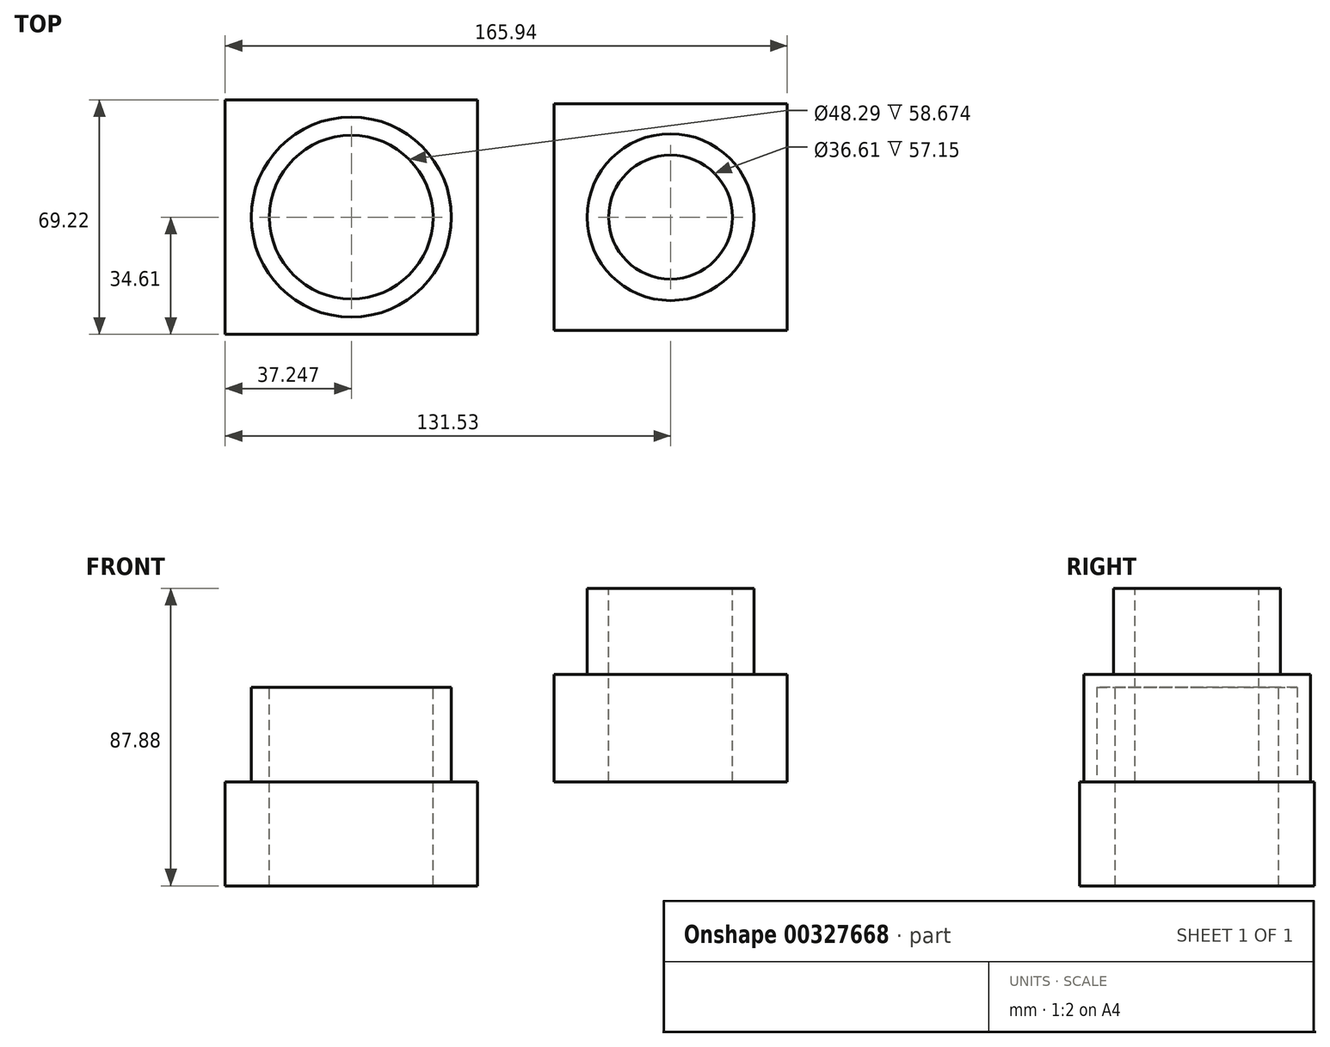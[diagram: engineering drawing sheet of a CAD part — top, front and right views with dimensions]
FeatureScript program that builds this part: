
annotation { "Feature Type Name" : "Feature", "Feature Type Description" : "" }
export const myFeature = defineFeature(function(context is Context, id is Id, definition is map)
    precondition{}
    {
        {
            var Q0;
            Q0=qCreatedBy(makeId("Top.planeOp"),FACE);
            var sketch = newSketch(context, id + "F0", { "sketchPlane" : qUnion([Q0])});
            skLineSegment(sketch, "E0.bottom", {"start": v(-34.4, -33.47) * mm, "end": v(34.4, -33.47) * mm});
            skLineSegment(sketch, "E0.top", {"start": v(-34.4, 33.47) * mm, "end": v(34.4, 33.47) * mm});
            skLineSegment(sketch, "E0.left", {"start": v(-34.4, -33.47) * mm, "end": v(-34.4, 33.47) * mm});
            skLineSegment(sketch, "E0.right", {"start": v(34.4, -33.47) * mm, "end": v(34.4, 33.47) * mm});
            skPoint(sketch, "E0.middle", {"position": v(0, 0) * mm});
            skSolve(sketch);
        }
        {
            var Q0;
            Q0 = qSketchRegion(id + "F0", true);
            extrude(context, id + "F1", {"entities" : qUnion([Q0]), "depth" : 31.75 * mm});
        }
        {
            var Q0;
            Q0=makeQuery(id+"F1.opExtrude","CAP_FACE",FACE,{"disambiguationData":[OSD([sQuery(id+"F0.wireOp",EDGE,"E0.bottom"),sQuery(id+"F0.wireOp",EDGE,"E0.top"),sQuery(id+"F0.wireOp",EDGE,"E0.left"),sQuery(id+"F0.wireOp",EDGE,"E0.right")])],"isStart":false});
            var sketch = newSketch(context, id + "F2", { "sketchPlane" : qUnion([Q0])});
            skCircle(sketch, "E1", {"center": v(0, 0) * mm, "radius": 18.3 * mm});
            skSolve(sketch);
        }
        {
            var Q0;
            Q0 = qSketchRegion(id + "F2", true);
            extrude(context, id + "F3", {"entities" : qUnion([Q0]), "operationType" : NewBodyOperationType.REMOVE, "oppositeDirection" : true, "depth" : 140.46 * mm});
        }
        {
            var Q0;
            Q0=makeQuery(id+"F1.opExtrude","CAP_FACE",FACE,{"disambiguationData":[OSD([sQuery(id+"F0.wireOp",EDGE,"E0.bottom"),sQuery(id+"F0.wireOp",EDGE,"E0.top"),sQuery(id+"F0.wireOp",EDGE,"E0.left"),sQuery(id+"F0.wireOp",EDGE,"E0.right")])],"isStart":false});
            var sketch = newSketch(context, id + "F4", { "sketchPlane" : qUnion([Q0])});
            skCircle(sketch, "E2", {"center": v(0, 0) * mm, "radius": 24.63 * mm});
            skSolve(sketch);
        }
        {
            var Q0;
            Q0=makeQuery(id+"F4.imprint","IMPRINT",FACE,{"disambiguationData":[TD([[makeQuery(id+"F4.imprint","IMPRINT",EDGE,{"derivedFrom":sQuery(id+"F4.wireOp",EDGE,"E2")}),1.0]])]});
            extrude(context, id + "F5", {"entities" : qUnion([Q0]), "operationType" : NewBodyOperationType.ADD, "depth" : 25.4 * mm});
        }
        {
            var Q0;
            Q0=qCreatedBy(makeId("Top.planeOp"),FACE);
            var sketch = newSketch(context, id + "F6", { "sketchPlane" : qUnion([Q0])});
            skLineSegment(sketch, "E3.bottom", {"start": v(-57.03, -34.61) * mm, "end": v(-131.53, -34.61) * mm});
            skLineSegment(sketch, "E3.top", {"start": v(-57.03, 34.61) * mm, "end": v(-131.53, 34.61) * mm});
            skLineSegment(sketch, "E3.left", {"start": v(-57.03, -34.61) * mm, "end": v(-57.03, 34.61) * mm});
            skLineSegment(sketch, "E3.right", {"start": v(-131.53, -34.61) * mm, "end": v(-131.53, 34.61) * mm});
            skPoint(sketch, "E3.middle", {"position": v(-94.28, 0) * mm});
            skCircle(sketch, "E4", {"center": v(-94.28, 0) * mm, "radius": 24.15 * mm});
            skSolve(sketch);
        }
        {
            var Q0;
            Q0=makeQuery(id+"F6.imprint","IMPRINT",FACE,{"disambiguationData":[TD([[makeQuery(id+"F6.imprint","IMPRINT",EDGE,{"derivedFrom":sQuery(id+"F6.wireOp",EDGE,"E3.bottom")}),-1.0]])]});
            extrude(context, id + "F7", {"entities" : qUnion([Q0]), "oppositeDirection" : true, "depth" : 30.73 * mm});
        }
        {
            var Q0;
            Q0=makeQuery(id+"F7.opExtrude","CAP_FACE",FACE,{"disambiguationData":[OSD([sQuery(id+"F6.wireOp",EDGE,"E3.bottom"),sQuery(id+"F6.wireOp",EDGE,"E3.top"),sQuery(id+"F6.wireOp",EDGE,"E3.left"),sQuery(id+"F6.wireOp",EDGE,"E3.right"),sQuery(id+"F6.wireOp",EDGE,"E4")])],"isStart":true});
            var sketch = newSketch(context, id + "F8", { "sketchPlane" : qUnion([Q0])});
            skCircle(sketch, "E5", {"center": v(-94.28, 0) * mm, "radius": 29.54 * mm});
            skSolve(sketch);
        }
        {
            var Q0;
            Q0=makeQuery(id+"F8.imprint","IMPRINT",FACE,{"disambiguationData":[TD([[makeQuery(id+"F8.imprint","IMPRINT",EDGE,{"derivedFrom":sQuery(id+"F8.wireOp",EDGE,"E5")}),1.0]])]});
            var sketch = newSketch(context, id + "F9", { "sketchPlane" : qUnion([Q0])});
            skCircle(sketch, "E6.0", {"center": v(-94.28, 0) * mm, "radius": 24.15 * mm});
            skCircle(sketch, "E7.0", {"center": v(-94.28, 0) * mm, "radius": 29.54 * mm});
            skSolve(sketch);
        }
        {
            var Q0;
            Q0 = qSketchRegion(id + "F9", true);
            extrude(context, id + "F10", {"entities" : qUnion([Q0]), "operationType" : NewBodyOperationType.ADD, "endBound" : BoundingType.SYMMETRIC, "depth" : 55.88 * mm});
        }
    });
